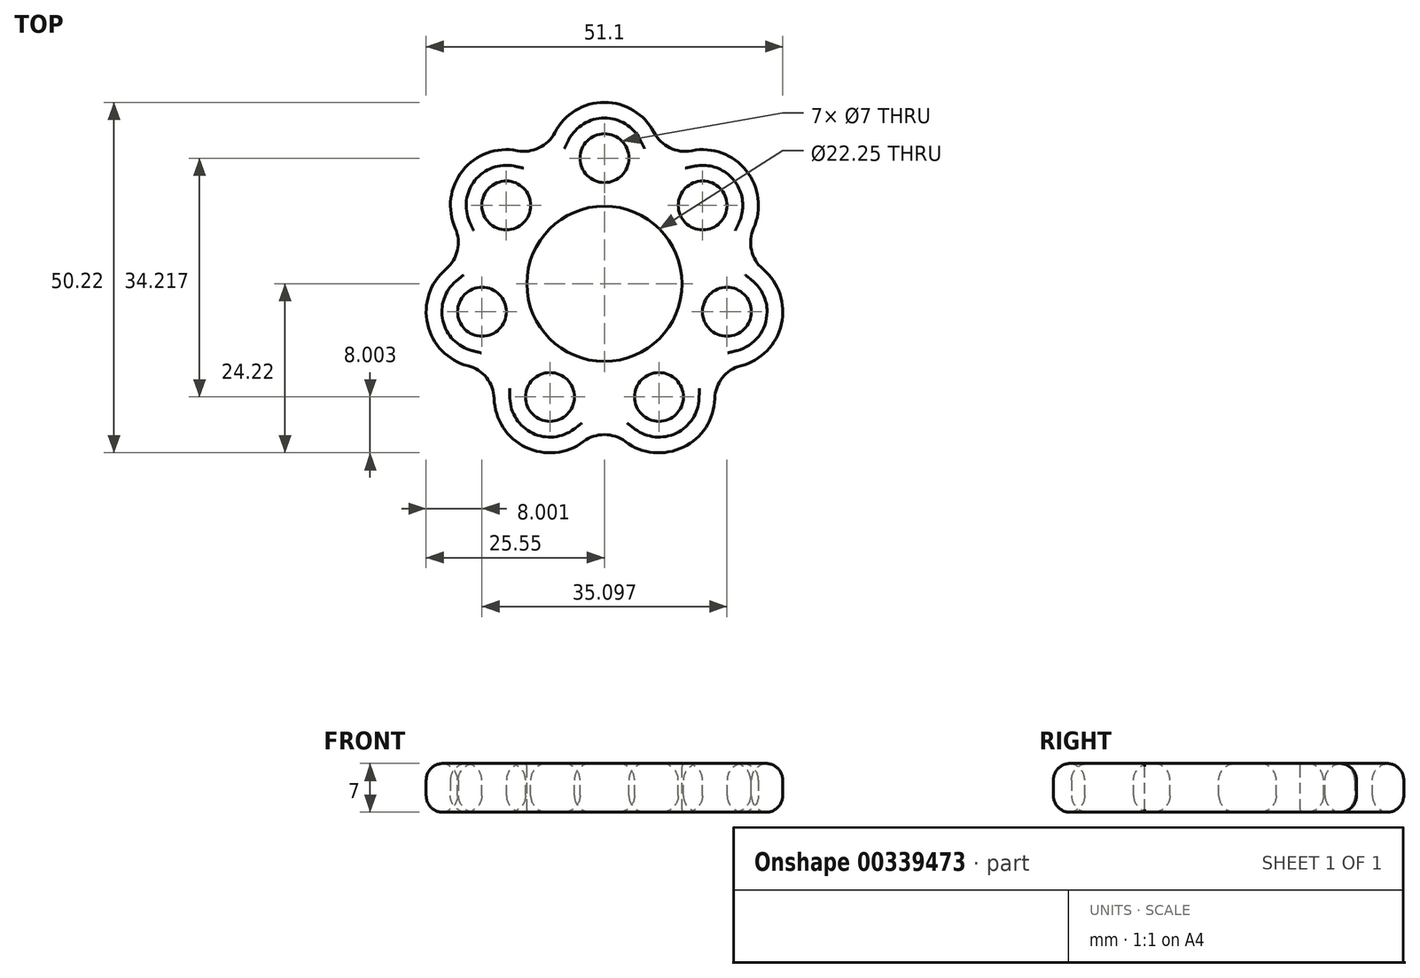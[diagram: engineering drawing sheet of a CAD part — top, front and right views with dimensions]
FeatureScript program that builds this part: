
annotation { "Feature Type Name" : "Feature", "Feature Type Description" : "" }
export const myFeature = defineFeature(function(context is Context, id is Id, definition is map)
    precondition{}
    {
        {
            var Q0;
            Q0=qCreatedBy(makeId("Top.planeOp"),FACE);
            var sketch = newSketch(context, id + "F0", { "sketchPlane" : qUnion([Q0])});
            skCircle(sketch, "E0", {"center": v(0, 0) * mm, "radius": 18 * mm, "construction": true});
            skArc(sketch, "E1", {"start": v(7.1, 21.68) * mm, "mid": v(0, 26) * mm, "end": v(-7.1, 21.68) * mm});
            skArc(sketch, "E2.1.0", {"start": v(-12.52, 19.07) * mm, "mid": v(-20.33, 16.21) * mm, "end": v(-21.38, 7.96) * mm});
            skArc(sketch, "E2.2.0", {"start": v(-22.71, 2.1) * mm, "mid": v(-25.35, -5.79) * mm, "end": v(-19.55, -11.75) * mm});
            skArc(sketch, "E2.3.0", {"start": v(-15.8, -16.45) * mm, "mid": v(-11.28, -23.43) * mm, "end": v(-3, -22.61) * mm});
            skArc(sketch, "E2.4.0", {"start": v(3, -22.61) * mm, "mid": v(11.28, -23.43) * mm, "end": v(15.8, -16.45) * mm});
            skArc(sketch, "E2.5.0", {"start": v(19.55, -11.75) * mm, "mid": v(25.35, -5.79) * mm, "end": v(22.71, 2.1) * mm});
            skArc(sketch, "E2.6.0", {"start": v(21.38, 7.96) * mm, "mid": v(20.33, 16.21) * mm, "end": v(12.52, 19.07) * mm});
            skPoint(sketch, "E3.visualSharp", {"position": v(-7.79, 16.17) * mm});
            skArc(sketch, "E3.filletArc", {"start": v(-12.52, 19.07) * mm, "mid": v(-9.38, 19.47) * mm, "end": v(-7.1, 21.68) * mm});
            skPoint(sketch, "E4.visualSharp", {"position": v(7.79, 16.17) * mm});
            skArc(sketch, "E4.filletArc", {"start": v(7.1, 21.68) * mm, "mid": v(9.38, 19.47) * mm, "end": v(12.52, 19.07) * mm});
            skPoint(sketch, "E5.visualSharp", {"position": v(17.5, 4) * mm});
            skArc(sketch, "E5.filletArc", {"start": v(21.38, 7.96) * mm, "mid": v(21.07, 4.8) * mm, "end": v(22.71, 2.1) * mm});
            skPoint(sketch, "E6.visualSharp", {"position": v(14.03, -11.2) * mm});
            skArc(sketch, "E6.filletArc", {"start": v(19.55, -11.75) * mm, "mid": v(16.9, -13.47) * mm, "end": v(15.8, -16.45) * mm});
            skPoint(sketch, "E7.visualSharp", {"position": v(0, -17.95) * mm});
            skArc(sketch, "E7.filletArc", {"start": v(3, -22.61) * mm, "mid": v(0, -21.61) * mm, "end": v(-3, -22.61) * mm});
            skPoint(sketch, "E8.visualSharp", {"position": v(-14.03, -11.2) * mm});
            skArc(sketch, "E8.filletArc", {"start": v(-15.8, -16.45) * mm, "mid": v(-16.9, -13.47) * mm, "end": v(-19.55, -11.75) * mm});
            skPoint(sketch, "E9.visualSharp", {"position": v(-17.5, 4) * mm});
            skArc(sketch, "E9.filletArc", {"start": v(-22.71, 2.1) * mm, "mid": v(-21.07, 4.8) * mm, "end": v(-21.38, 7.96) * mm});
            skSolve(sketch);
        }
        {
            var Q0;
            Q0 = qSketchRegion(id + "F0", true);
            extrude(context, id + "F1", {"entities" : qUnion([Q0]), "depth" : 7 * mm});
        }
        {
            var Q0;
            Q0=makeQuery(id+"F1.opExtrude","CAP_FACE",FACE,{"disambiguationData":[OSD([sQuery(id+"F0.wireOp",EDGE,"E1"),sQuery(id+"F0.wireOp",EDGE,"E2.1.0"),sQuery(id+"F0.wireOp",EDGE,"E2.2.0"),sQuery(id+"F0.wireOp",EDGE,"E2.3.0"),sQuery(id+"F0.wireOp",EDGE,"E2.4.0"),sQuery(id+"F0.wireOp",EDGE,"E2.5.0"),sQuery(id+"F0.wireOp",EDGE,"E2.6.0"),sQuery(id+"F0.wireOp",EDGE,"E3.filletArc"),sQuery(id+"F0.wireOp",EDGE,"E4.filletArc"),sQuery(id+"F0.wireOp",EDGE,"E5.filletArc"),sQuery(id+"F0.wireOp",EDGE,"E6.filletArc"),sQuery(id+"F0.wireOp",EDGE,"E7.filletArc"),sQuery(id+"F0.wireOp",EDGE,"E8.filletArc"),sQuery(id+"F0.wireOp",EDGE,"E9.filletArc")])],"isStart":false});
            var sketch = newSketch(context, id + "F2", { "sketchPlane" : qUnion([Q0])});
            skCircle(sketch, "E10", {"center": v(0, 0) * mm, "radius": 11.12 * mm});
            skSolve(sketch);
        }
        {
            var Q0;
            Q0 = qSketchRegion(id + "F2", true);
            extrude(context, id + "F3", {"entities" : qUnion([Q0]), "operationType" : NewBodyOperationType.REMOVE, "endBound" : BoundingType.THROUGH_ALL, "oppositeDirection" : true, "depth" : 25 * mm});
        }
        {
            var Q0;
            Q0=makeQuery(id+"F1.opExtrude","CAP_FACE",FACE,{"disambiguationData":[OSD([sQuery(id+"F0.wireOp",EDGE,"E1"),sQuery(id+"F0.wireOp",EDGE,"E2.1.0"),sQuery(id+"F0.wireOp",EDGE,"E2.2.0"),sQuery(id+"F0.wireOp",EDGE,"E2.3.0"),sQuery(id+"F0.wireOp",EDGE,"E2.4.0"),sQuery(id+"F0.wireOp",EDGE,"E2.5.0"),sQuery(id+"F0.wireOp",EDGE,"E2.6.0"),sQuery(id+"F0.wireOp",EDGE,"E3.filletArc"),sQuery(id+"F0.wireOp",EDGE,"E4.filletArc"),sQuery(id+"F0.wireOp",EDGE,"E5.filletArc"),sQuery(id+"F0.wireOp",EDGE,"E6.filletArc"),sQuery(id+"F0.wireOp",EDGE,"E7.filletArc"),sQuery(id+"F0.wireOp",EDGE,"E8.filletArc"),sQuery(id+"F0.wireOp",EDGE,"E9.filletArc")])],"isStart":false});
            var sketch = newSketch(context, id + "F4", { "sketchPlane" : qUnion([Q0])});
            skCircle(sketch, "E11", {"center": v(0, 18) * mm, "radius": 3.5 * mm});
            skCircle(sketch, "E12.1.0", {"center": v(-14.07, 11.22) * mm, "radius": 3.5 * mm});
            skCircle(sketch, "E12.2.0", {"center": v(-17.55, -4) * mm, "radius": 3.5 * mm});
            skCircle(sketch, "E12.3.0", {"center": v(-7.8, -16.22) * mm, "radius": 3.5 * mm});
            skCircle(sketch, "E12.4.0", {"center": v(7.8, -16.22) * mm, "radius": 3.5 * mm});
            skCircle(sketch, "E12.5.0", {"center": v(17.55, -4) * mm, "radius": 3.5 * mm});
            skCircle(sketch, "E12.6.0", {"center": v(14.07, 11.22) * mm, "radius": 3.5 * mm});
            skPoint(sketch, "E12.center", {"position": v(0, 0) * mm});
            skSolve(sketch);
        }
        {
            var Q0;
            Q0 = qSketchRegion(id + "F4", true);
            extrude(context, id + "F5", {"entities" : qUnion([Q0]), "operationType" : NewBodyOperationType.REMOVE, "endBound" : BoundingType.THROUGH_ALL, "oppositeDirection" : true, "depth" : 25 * mm});
        }
        {
            var Q0;
            Q0=makeQuery(id+"F3.boolean.opBoolean","COPY",FACE,{"derivedFrom":makeQuery(id+"F3.opExtrude","SWEPT_FACE",FACE,{"disambiguationData":[OSD([sQuery(id+"F2.wireOp",EDGE,"E10")])]})});
            fillet(context, id + "F6", {"entities" : qUnion([Q0]), "radius" : .4 * mm, "tangentPropagation" : true, "allowEdgeOverflow" : false});
        }
        {
            var Q0;
            Q0=makeQuery(id+"F1.opExtrude","CAP_FACE",FACE,{"disambiguationData":[OSD([sQuery(id+"F0.wireOp",EDGE,"E1"),sQuery(id+"F0.wireOp",EDGE,"E2.1.0"),sQuery(id+"F0.wireOp",EDGE,"E2.2.0"),sQuery(id+"F0.wireOp",EDGE,"E2.3.0"),sQuery(id+"F0.wireOp",EDGE,"E2.4.0"),sQuery(id+"F0.wireOp",EDGE,"E2.5.0"),sQuery(id+"F0.wireOp",EDGE,"E2.6.0"),sQuery(id+"F0.wireOp",EDGE,"E3.filletArc"),sQuery(id+"F0.wireOp",EDGE,"E4.filletArc"),sQuery(id+"F0.wireOp",EDGE,"E5.filletArc"),sQuery(id+"F0.wireOp",EDGE,"E6.filletArc"),sQuery(id+"F0.wireOp",EDGE,"E7.filletArc"),sQuery(id+"F0.wireOp",EDGE,"E8.filletArc"),sQuery(id+"F0.wireOp",EDGE,"E9.filletArc")])],"isStart":false});
            var Q1;
            Q1=makeQuery(id+"F1.opExtrude","CAP_FACE",FACE,{"disambiguationData":[OSD([sQuery(id+"F0.wireOp",EDGE,"E1"),sQuery(id+"F0.wireOp",EDGE,"E2.1.0"),sQuery(id+"F0.wireOp",EDGE,"E2.2.0"),sQuery(id+"F0.wireOp",EDGE,"E2.3.0"),sQuery(id+"F0.wireOp",EDGE,"E2.4.0"),sQuery(id+"F0.wireOp",EDGE,"E2.5.0"),sQuery(id+"F0.wireOp",EDGE,"E2.6.0"),sQuery(id+"F0.wireOp",EDGE,"E3.filletArc"),sQuery(id+"F0.wireOp",EDGE,"E4.filletArc"),sQuery(id+"F0.wireOp",EDGE,"E5.filletArc"),sQuery(id+"F0.wireOp",EDGE,"E6.filletArc"),sQuery(id+"F0.wireOp",EDGE,"E7.filletArc"),sQuery(id+"F0.wireOp",EDGE,"E8.filletArc"),sQuery(id+"F0.wireOp",EDGE,"E9.filletArc")])],"isStart":true});
            fillet(context, id + "F7", {"entities" : qUnion([Q0, Q1]), "radius" : 2.4 * mm, "tangentPropagation" : true, "allowEdgeOverflow" : false});
        }
    });
